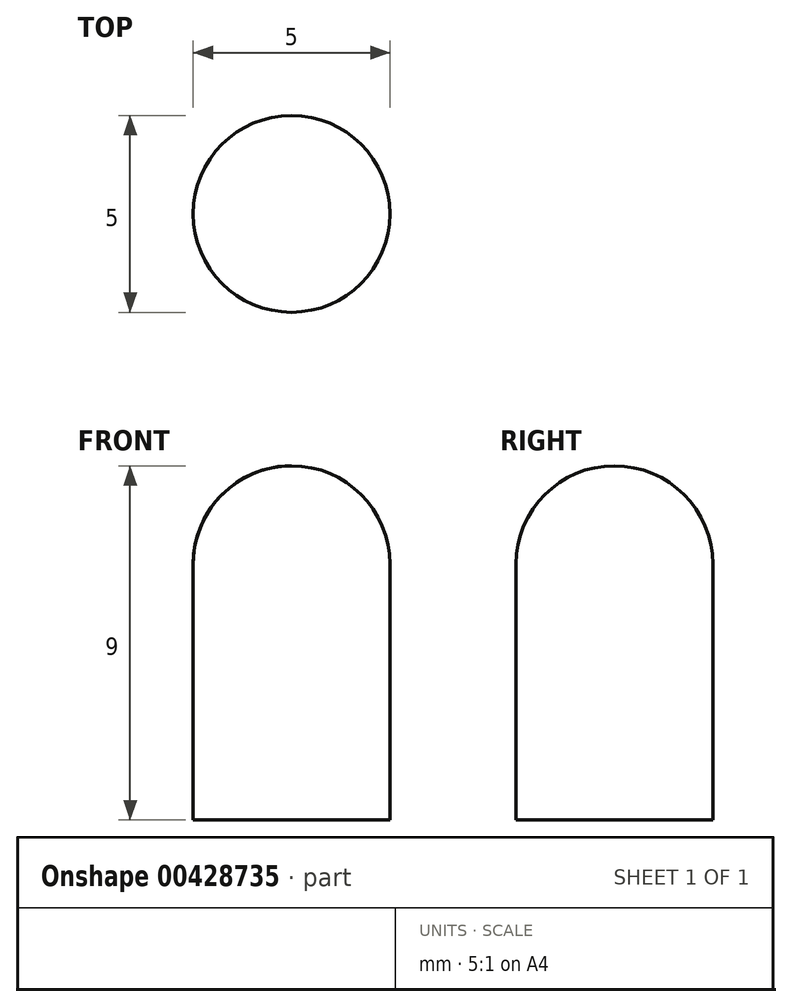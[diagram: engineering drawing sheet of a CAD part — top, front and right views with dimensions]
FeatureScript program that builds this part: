
annotation { "Feature Type Name" : "Feature", "Feature Type Description" : "" }
export const myFeature = defineFeature(function(context is Context, id is Id, definition is map)
    precondition{}
    {
        {
            var Q0;
            Q0=qCreatedBy(makeId("Front.planeOp"),FACE);
            var sketch = newSketch(context, id + "F0", { "sketchPlane" : qUnion([Q0])});
            skLineSegment(sketch, "E0", {"start": v(0, 9) * mm, "end": v(0, 0) * mm});
            skLineSegment(sketch, "E1", {"start": v(0, 0) * mm, "end": v(-2.5, 0) * mm});
            skLineSegment(sketch, "E2", {"start": v(-2.5, 0) * mm, "end": v(-2.5, 6.5) * mm});
            skArc(sketch, "E3", {"start": v(-2.5, 6.5) * mm, "mid": v(-1.77, 8.27) * mm, "end": v(0, 9) * mm});
            skSolve(sketch);
        }
        {
            var Q0;
            Q0=makeQuery(id+"F0.imprint","IMPRINT",FACE,{"disambiguationData":[TD([[makeQuery(id+"F0.imprint","IMPRINT",EDGE,{"derivedFrom":sQuery(id+"F0.wireOp",EDGE,"E0")}),-1.0]])]});
            var Q1;
            Q1=sQuery(id+"F0.wireOp",EDGE,"E0");
            revolve(context, id + "F1", {"entities" : qUnion([Q0]), "axis" : qUnion([Q1]), "revolveType" : RevolveType.FULL});
        }
    });
